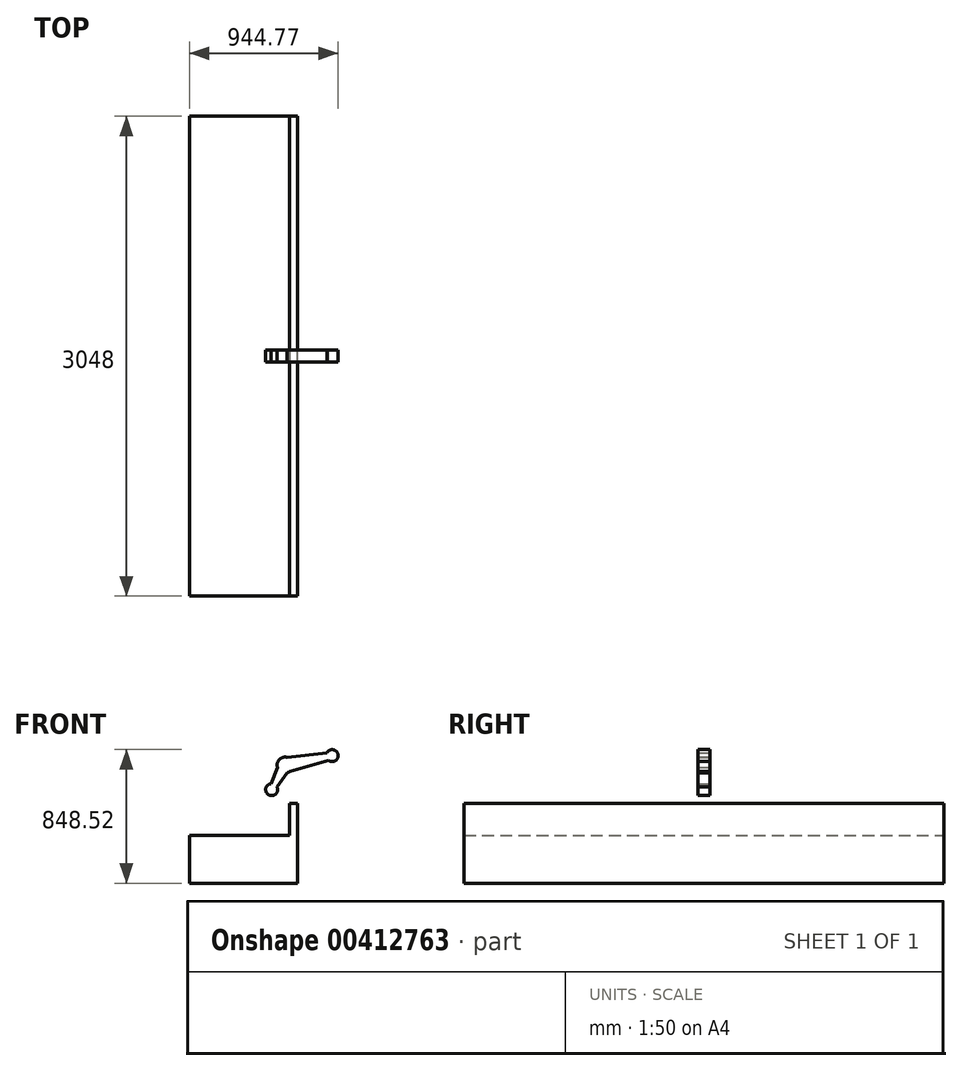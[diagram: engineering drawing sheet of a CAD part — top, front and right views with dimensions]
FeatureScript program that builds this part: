
annotation { "Feature Type Name" : "Feature", "Feature Type Description" : "" }
export const myFeature = defineFeature(function(context is Context, id is Id, definition is map)
    precondition{}
    {
        {
            var Q0;
            Q0=qCreatedBy(makeId("Front.planeOp"),FACE);
            var sketch = newSketch(context, id + "F0", { "sketchPlane" : qUnion([Q0])});
            skLineSegment(sketch, "E0", {"start": v(-635, 0) * mm, "end": v(0, 0) * mm});
            skLineSegment(sketch, "E1", {"start": v(0, 0) * mm, "end": v(0, 203.2) * mm});
            skLineSegment(sketch, "E2", {"start": v(0, 203.2) * mm, "end": v(50.8, 203.2) * mm});
            skLineSegment(sketch, "E3", {"start": v(50.8, 203.2) * mm, "end": v(50.8, -304.8) * mm});
            skLineSegment(sketch, "E4", {"start": v(50.8, -304.8) * mm, "end": v(-635, -304.8) * mm});
            skLineSegment(sketch, "E5", {"start": v(-635, -304.8) * mm, "end": v(-635, 0) * mm});
            skSolve(sketch);
        }
        {
            var Q0;
            Q0=makeQuery(id+"F0.imprint","IMPRINT",FACE,{"disambiguationData":[TD([[makeQuery(id+"F0.imprint","IMPRINT",EDGE,{"derivedFrom":sQuery(id+"F0.wireOp",EDGE,"E0")}),-1.0]])]});
            extrude(context, id + "F1", {"entities" : qUnion([Q0]), "endBound" : BoundingType.SYMMETRIC, "depth" : 3048 * mm});
        }
        {
            var Q0;
            Q0=qCreatedBy(makeId("Front.planeOp"),FACE);
            var sketch = newSketch(context, id + "F2", { "sketchPlane" : qUnion([Q0])});
            skCircle(sketch, "E6", {"center": v(-112.4, 289.59) * mm, "radius": 38.1 * mm});
            skCircle(sketch, "E7", {"center": v(-27.16, 445.62) * mm, "radius": 50.8 * mm});
            skCircle(sketch, "E8", {"center": v(271.67, 505.62) * mm, "radius": 38.1 * mm});
            skLineSegment(sketch, "E9", {"start": v(-112.4, 289.59) * mm, "end": v(-27.16, 445.62) * mm, "construction": true});
            skLineSegment(sketch, "E10", {"start": v(271.67, 505.62) * mm, "end": v(-27.16, 445.62) * mm, "construction": true});
            skLineSegment(sketch, "E11", {"start": v(-117.08, 327.4) * mm, "end": v(-75.36, 429.56) * mm});
            skLineSegment(sketch, "E12", {"start": v(-78.06, 306.08) * mm, "end": v(-14.64, 396.4) * mm});
            skLineSegment(sketch, "E13", {"start": v(-13.76, 494.62) * mm, "end": v(237.86, 523.18) * mm});
            skLineSegment(sketch, "E14", {"start": v(4.12, 405.6) * mm, "end": v(247.26, 476.37) * mm});
            skSolve(sketch);
        }
        {
            var Q0;
            {var subQ0=sQuery(id+"F2.wireOp",EDGE,"E7");var subQ1=makeQuery(id+"F2.imprint","INTERSECT",VERTEX,{"derivedFrom":[subQ0,sQuery(id+"F2.wireOp",EDGE,"E11")]});Q0=makeQuery(id+"F2.imprint","IMPRINT",FACE,{"disambiguationData":[TD([[makeQuery(id+"F2.imprint","IMPRINT",EDGE,{"disambiguationData":[TD([[subQ1,1.0]])],"derivedFrom":subQ0}),1.0]])]});}
            var Q1;
            {var subQ0=sQuery(id+"F2.wireOp",EDGE,"E13");Q1=makeQuery(id+"F2.imprint","IMPRINT",FACE,{"disambiguationData":[TD([[makeQuery(id+"F2.imprint","IMPRINT",EDGE,{"derivedFrom":subQ0}),-1.0]])]});}
            var Q2;
            {var subQ0=sQuery(id+"F2.wireOp",EDGE,"E8");var subQ1=makeQuery(id+"F2.imprint","INTERSECT",VERTEX,{"derivedFrom":[subQ0,sQuery(id+"F2.wireOp",EDGE,"E13")]});Q2=makeQuery(id+"F2.imprint","IMPRINT",FACE,{"disambiguationData":[TD([[makeQuery(id+"F2.imprint","IMPRINT",EDGE,{"disambiguationData":[TD([[subQ1,-1.0]])],"derivedFrom":subQ0}),1.0]])]});}
            var Q3;
            {var subQ0=sQuery(id+"F2.wireOp",EDGE,"E6");var subQ1=makeQuery(id+"F2.imprint","INTERSECT",VERTEX,{"derivedFrom":[subQ0,sQuery(id+"F2.wireOp",EDGE,"E11")]});Q3=makeQuery(id+"F2.imprint","IMPRINT",FACE,{"disambiguationData":[TD([[makeQuery(id+"F2.imprint","IMPRINT",EDGE,{"disambiguationData":[TD([[subQ1,1.0]])],"derivedFrom":subQ0}),1.0]])]});}
            var Q4;
            {var subQ0=sQuery(id+"F2.wireOp",EDGE,"E11");Q4=makeQuery(id+"F2.imprint","IMPRINT",FACE,{"disambiguationData":[TD([[makeQuery(id+"F2.imprint","IMPRINT",EDGE,{"derivedFrom":subQ0}),-1.0]])]});}
            extrude(context, id + "F3", {"entities" : qUnion([Q0, Q1, Q2, Q3, Q4]), "endBound" : BoundingType.SYMMETRIC, "depth" : 76.2 * mm});
        }
        {
            var Q0;
            Q0=qCreatedBy(makeId("Front.planeOp"),FACE);
            var sketch = newSketch(context, id + "F4", { "sketchPlane" : qUnion([Q0])});
            skArc(sketch, "E15.0", {"start": v(-147.06, 305.42) * mm, "mid": v(-138.2, 261.54) * mm, "end": v(-93.73, 256.38) * mm});
            skArc(sketch, "E16.0", {"start": v(290.35, 472.41) * mm, "mid": v(307.62, 518.26) * mm, "end": v(265.47, 543.21) * mm});
            skArc(sketch, "E17.0", {"start": v(-35.08, 495.8) * mm, "mid": v(-57.88, 486.08) * mm, "end": v(-73.37, 466.73) * mm});
            skLineSegment(sketch, "E18", {"start": v(265.47, 543.21) * mm, "end": v(-35.08, 495.8) * mm});
            skLineSegment(sketch, "E19", {"start": v(-147.06, 305.42) * mm, "end": v(-73.37, 466.73) * mm});
            skLineSegment(sketch, "E20", {"start": v(290.35, 472.41) * mm, "end": v(-93.73, 256.38) * mm});
            skArc(sketch, "E21", {"start": v(265.47, 543.21) * mm, "mid": v(307.62, 518.26) * mm, "end": v(290.35, 472.41) * mm});
            skPoint(sketch, "E22.orphan", {"position": v(-117.08, 327.4) * mm});
            skPoint(sketch, "E23.orphan", {"position": v(-78.06, 306.08) * mm});
            skPoint(sketch, "E24.orphan", {"position": v(-75.36, 429.56) * mm});
            skPoint(sketch, "E25.orphan", {"position": v(-13.76, 494.62) * mm});
            skPoint(sketch, "E26.orphan", {"position": v(237.86, 523.18) * mm});
            skPoint(sketch, "E27.orphan", {"position": v(247.26, 476.37) * mm});
            skSolve(sketch);
        }
        {
            var Q0;
            Q0=sQuery(id+"F4.wireOp",EDGE,"E19");
            var Q1;
            Q1=sQuery(id+"F4.wireOp",EDGE,"E15.0");
            var Q2;
            Q2=sQuery(id+"F4.wireOp",EDGE,"E20");
            var Q3;
            Q3=sQuery(id+"F4.wireOp",EDGE,"E21");
            var Q4;
            Q4=sQuery(id+"F4.wireOp",EDGE,"E18");
            var Q5;
            Q5=sQuery(id+"F4.wireOp",EDGE,"E17.0");
            extrude(context, id + "F5", {"bodyType" : ToolBodyType.SURFACE, "surfaceEntities" : qUnion([Q0, Q1, Q2, Q3, Q4, Q5]), "endBound" : BoundingType.SYMMETRIC, "depth" : 63.5 * mm});
        }
    });
